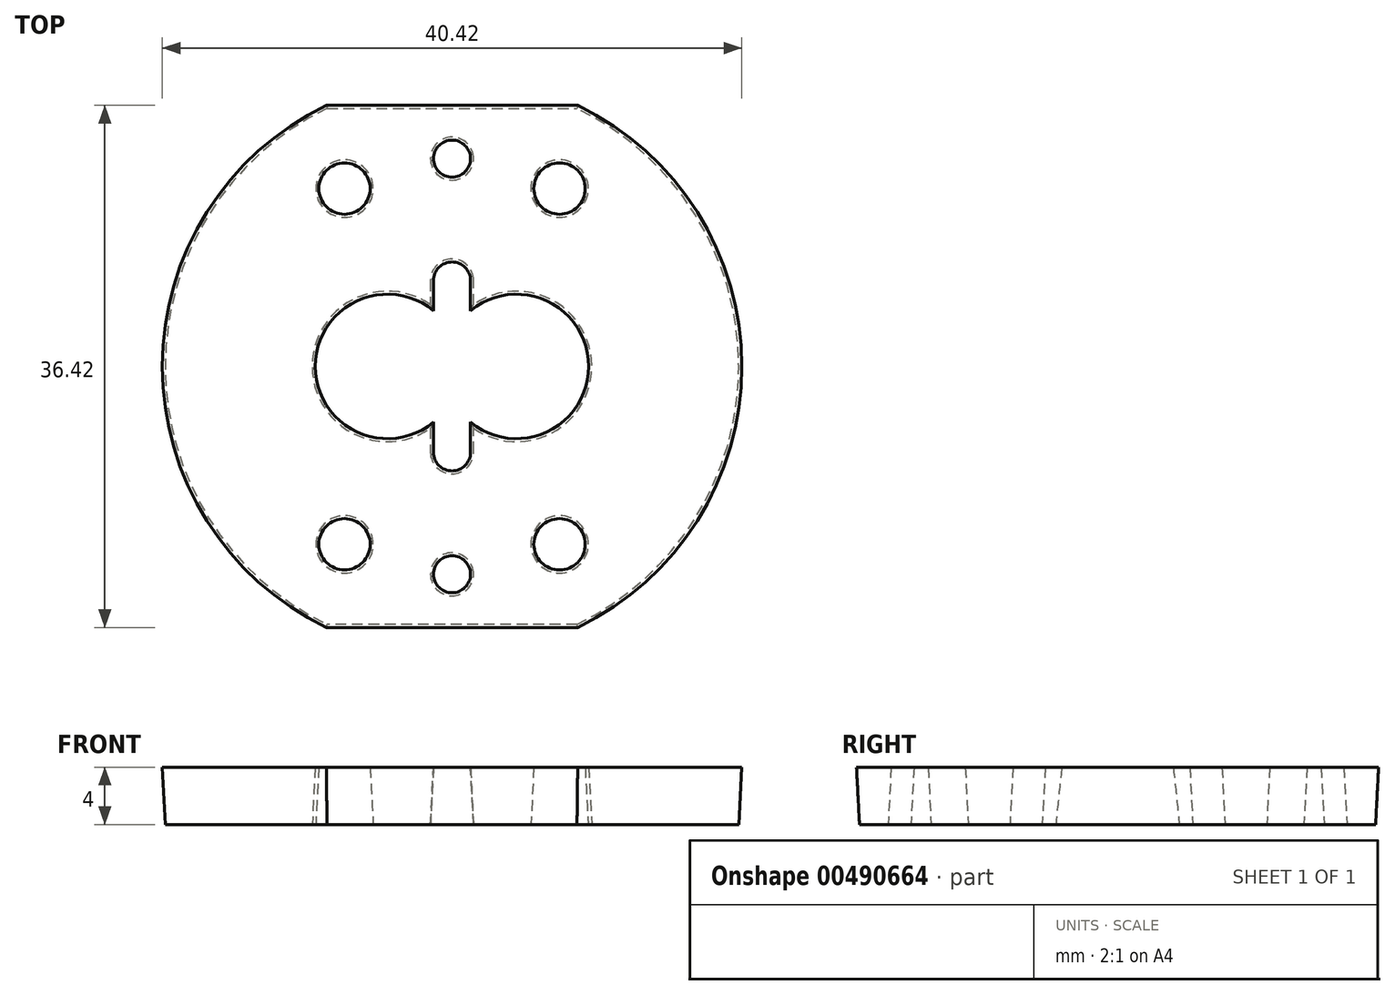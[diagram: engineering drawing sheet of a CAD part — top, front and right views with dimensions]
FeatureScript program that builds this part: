
annotation { "Feature Type Name" : "Feature", "Feature Type Description" : "" }
export const myFeature = defineFeature(function(context is Context, id is Id, definition is map)
    precondition{}
    {
        {
            var Q0;
            Q0=qCreatedBy(makeId("Top.planeOp"),FACE);
            var sketch = newSketch(context, id + "F0", { "sketchPlane" : qUnion([Q0])});
            skCircle(sketch, "E0", {"center": v(0, 0) * mm, "radius": 20 * mm});
            skLineSegment(sketch, "E1", {"start": v(0, 0) * mm, "end": v(4.5, 0) * mm, "construction": true});
            skLineSegment(sketch, "E2", {"start": v(0, 0) * mm, "end": v(-4.5, 0) * mm, "construction": true});
            skCircle(sketch, "E3", {"center": v(0, 0) * mm, "radius": 14.5 * mm, "construction": true});
            skCircle(sketch, "E4", {"center": v(-7.5, 12.4) * mm, "radius": 2 * mm});
            skCircle(sketch, "E5", {"center": v(7.5, 12.4) * mm, "radius": 2 * mm});
            skCircle(sketch, "E6", {"center": v(7.5, -12.4) * mm, "radius": 2 * mm});
            skCircle(sketch, "E7", {"center": v(-7.5, -12.4) * mm, "radius": 2 * mm});
            skLineSegment(sketch, "E8", {"start": v(0, 0) * mm, "end": v(0, 14.5) * mm, "construction": true});
            skLineSegment(sketch, "E9", {"start": v(0, 0) * mm, "end": v(0, -14.5) * mm, "construction": true});
            skCircle(sketch, "E10", {"center": v(0, 14.5) * mm, "radius": 1.5 * mm});
            skCircle(sketch, "E11", {"center": v(0, -14.5) * mm, "radius": 1.5 * mm});
            skCircle(sketch, "E12", {"center": v(4.5, 0) * mm, "radius": 5.25 * mm});
            skCircle(sketch, "E13", {"center": v(-4.5, 0) * mm, "radius": 5.25 * mm});
            skCircle(sketch, "E14", {"center": v(0, -6) * mm, "radius": 1.5 * mm});
            skCircle(sketch, "E15", {"center": v(0, 6) * mm, "radius": 1.5 * mm});
            skLineSegment(sketch, "E16", {"start": v(-1.5, 6) * mm, "end": v(-1.5, -6) * mm});
            skLineSegment(sketch, "E17", {"start": v(1.5, -6) * mm, "end": v(1.5, 6) * mm});
            skLineSegment(sketch, "E18", {"start": v(-7.5, -12.4) * mm, "end": v(-7.5, 12.4) * mm, "construction": true});
            skLineSegment(sketch, "E19", {"start": v(7.5, -12.4) * mm, "end": v(7.5, 12.4) * mm, "construction": true});
            skLineSegment(sketch, "E20", {"start": v(-8.72, 18) * mm, "end": v(8.72, 18) * mm});
            skLineSegment(sketch, "E21", {"start": v(-8.72, -18) * mm, "end": v(8.72, -18) * mm});
            skSolve(sketch);
        }
        {
            var Q0;
            Q0=makeQuery(id+"F0.imprint","IMPRINT",FACE,{"disambiguationData":[TD([[makeQuery(id+"F0.imprint","IMPRINT",EDGE,{"derivedFrom":sQuery(id+"F0.wireOp",EDGE,"E4")}),-1.0]])]});
            extrude(context, id + "F1", {"entities" : qUnion([Q0]), "depth" : 4 * mm, "hasDraft" : true, "draftAngle" : 3 * degree, "offsetDistance" : 25 * mm});
        }
    });
